# Revit family: 15HS000X Closed
name_source: partatom
category: Specialty Equipment
units: mm (PartAtom-declared; Revit-internal decimal feet)

## family parameters
Always vertical = Yes
Cut with Voids When Loaded = No
Host = Wall
Part Type = Normal
Room Calculation Point = No
Round Connector Dimension = Use Diameter
Shared = No

## types (1)
- 15HS000X Closed
    Configuration = Closed
    Description = Element Baby Changing Station With Liner Dispenser
    Elevation = 43
    Frame Finish = Stainless Steel Finish
    Height = 43 "
    Manufacturer = The Sova Company
    Material(s) = High Density Polyethylene (HDPE) and Chrome Plated Cold Rolled Steel
    Model = 15HS000X Closed
    Panel Finish = Stainless Steel Finish
    Product Site = https://choosesova.com
    Product Weight = 24lb
    SKU = 300-EHLD
    Shipping Height = 4.68 "
    Shipping Length = 38.81 "
    Shipping Width = 22.56 "
    URL = https://choosesova.com
    Unit Depth = 4 "
    Unit Height = 21 "
    Unit Length = 37.5 "
    Weight Capacity = 350lb

## geometry (parser evidence)
native form markers: Sweep x9
no freeform markers — native parametric forms only
